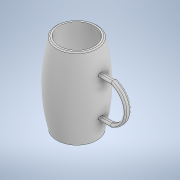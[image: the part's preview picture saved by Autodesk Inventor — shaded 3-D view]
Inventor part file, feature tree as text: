
AUTODESK INVENTOR PART (.ipt)
format: ipt  version: 2020 (Build 240168000, 168)  size: 231,424 bytes
history: native  units: mm
features: sketch x2, revolve x1, shell x1, extrude x1, fillet x1, chamfer x1
ambient origin geometry x8: Origin, YZ Plane, XZ Plane, XY Plane, X Axis, Y Axis, Z Axis, Center Point
bodies: Solid1 (feature_tree)
feature tree (7):
  revolve  "Revolution1"  [1 undecoded]
  shell  "Shell1"  Thickness=25.0mm
  extrude  "Extrusion1"  TaperAngle=90.0deg  [1 undecoded]
  fillet  "Fillet1"  Radius=2.5mm
  chamfer  "Chamfer1"  Distance=30.0mm
  sketch  "Sketch2"  dims[d4=34.0mm d6=45.0mm d7=25.0mm]
  sketch  "Sketch4"  dims[d8=80.0mm d9=90.0deg d10=2.5mm d11=30.0mm d12=40.0mm d13=3.0mm d14=6.0mm d15=0.0mm d16=2.0mm d17=1.0mm d18=2.0mm d19=45.0deg]
note: 2 required parameter values undecoded (feature->parameter linkage not recoverable at this tier; creation-order binding heuristic only, values carry confidence <= 0.55)